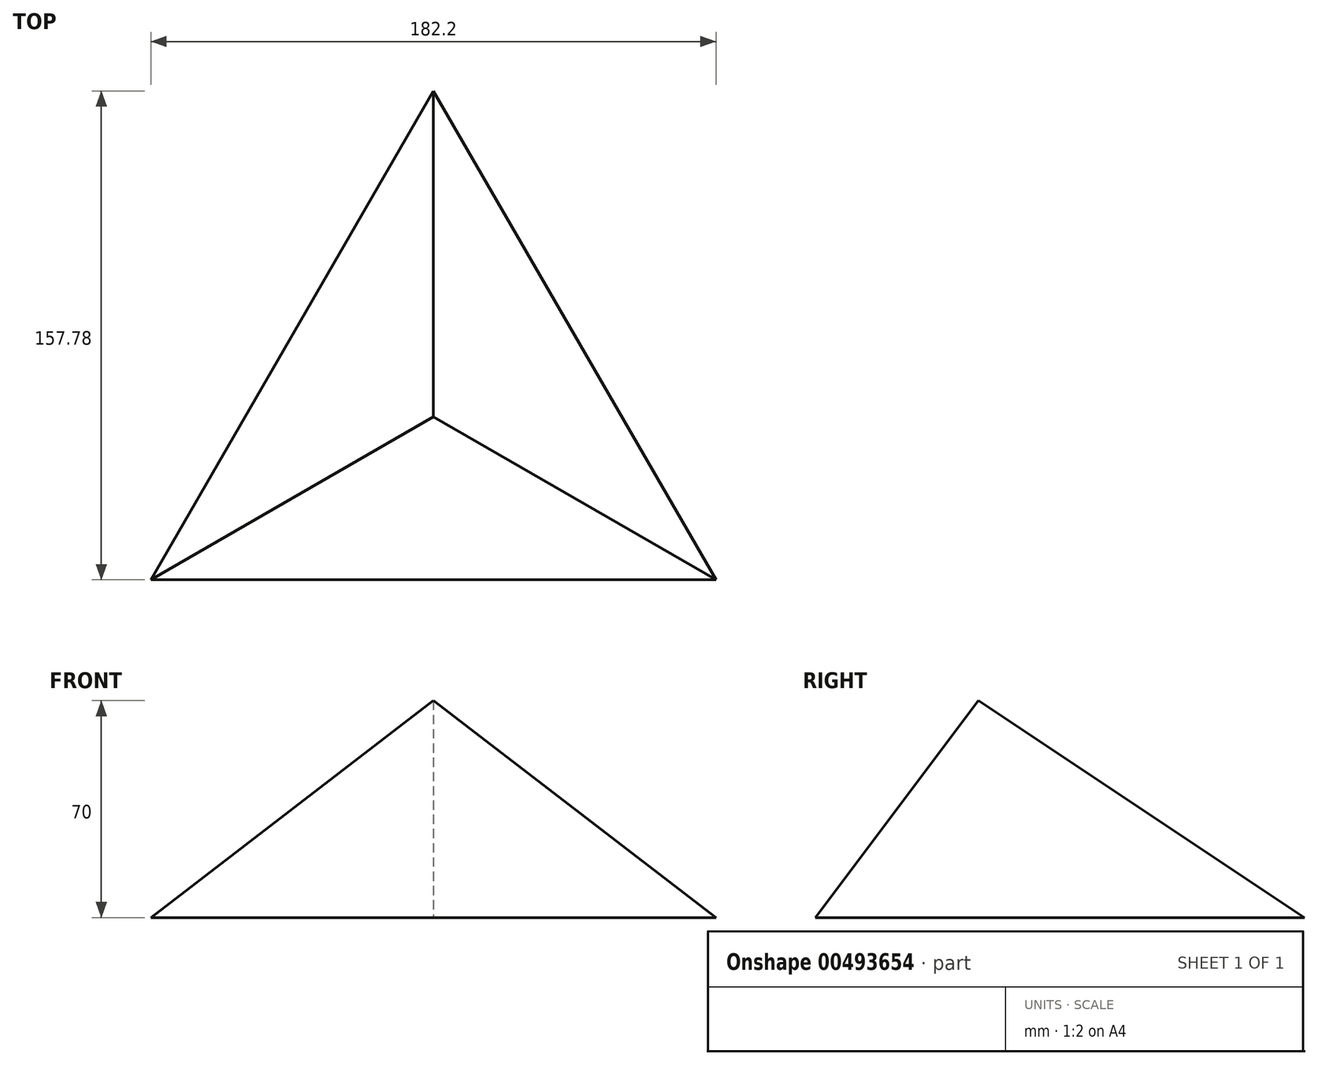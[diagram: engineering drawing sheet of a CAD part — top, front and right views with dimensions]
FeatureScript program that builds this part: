
annotation { "Feature Type Name" : "Feature", "Feature Type Description" : "" }
export const myFeature = defineFeature(function(context is Context, id is Id, definition is map)
    precondition{}
    {
        {
            var Q0;
            Q0=qCreatedBy(makeId("Top.planeOp"),FACE);
            var sketch = newSketch(context, id + "F0", { "sketchPlane" : qUnion([Q0])});
            skCircle(sketch, "E0.cCircle", {"center": v(0, 0) * mm, "radius": 105.19 * mm, "construction": true});
            skLineSegment(sketch, "E0.0", {"start": v(91.1, -52.6) * mm, "end": v(-91.1, -52.6) * mm});
            skLineSegment(sketch, "E0.1", {"start": v(-91.1, -52.6) * mm, "end": v(0, 105.19) * mm});
            skLineSegment(sketch, "E0.2", {"start": v(0, 105.19) * mm, "end": v(91.1, -52.6) * mm});
            skSolve(sketch);
        }
        {
            var Q0;
            Q0=qCreatedBy(makeId("Top.planeOp"),FACE);
            cPlane(context, id + "F1", {"entities" : qUnion([Q0]), "cplaneType" : CPlaneType.OFFSET, "offset" : 70 * mm, "width" : 150 * mm, "height" : 150 * mm});
        }
        {
            var Q0;
            Q0=qCreatedBy(id+"F1.planeOp",FACE);
            var sketch = newSketch(context, id + "F2", { "sketchPlane" : qUnion([Q0])});
            skPoint(sketch, "E1", {"position": v(0, 0) * mm});
            skSolve(sketch);
        }
        {
            var Q0;
            Q0=sQuery(id+"F2.wireOp",VERTEX,"E1");
            var Q1;
            Q1=makeQuery(id+"F0.imprint","IMPRINT",FACE,{"disambiguationData":[TD([[makeQuery(id+"F0.imprint","IMPRINT",EDGE,{"derivedFrom":sQuery(id+"F0.wireOp",EDGE,"E0.0")}),-1.0]])]});
            loft(context, id + "F3", {"sheetProfilesArray" : [{ "sheetProfileEntities" : qUnion([Q0]) }, { "sheetProfileEntities" : qUnion([Q1]) }]});
        }
    });
